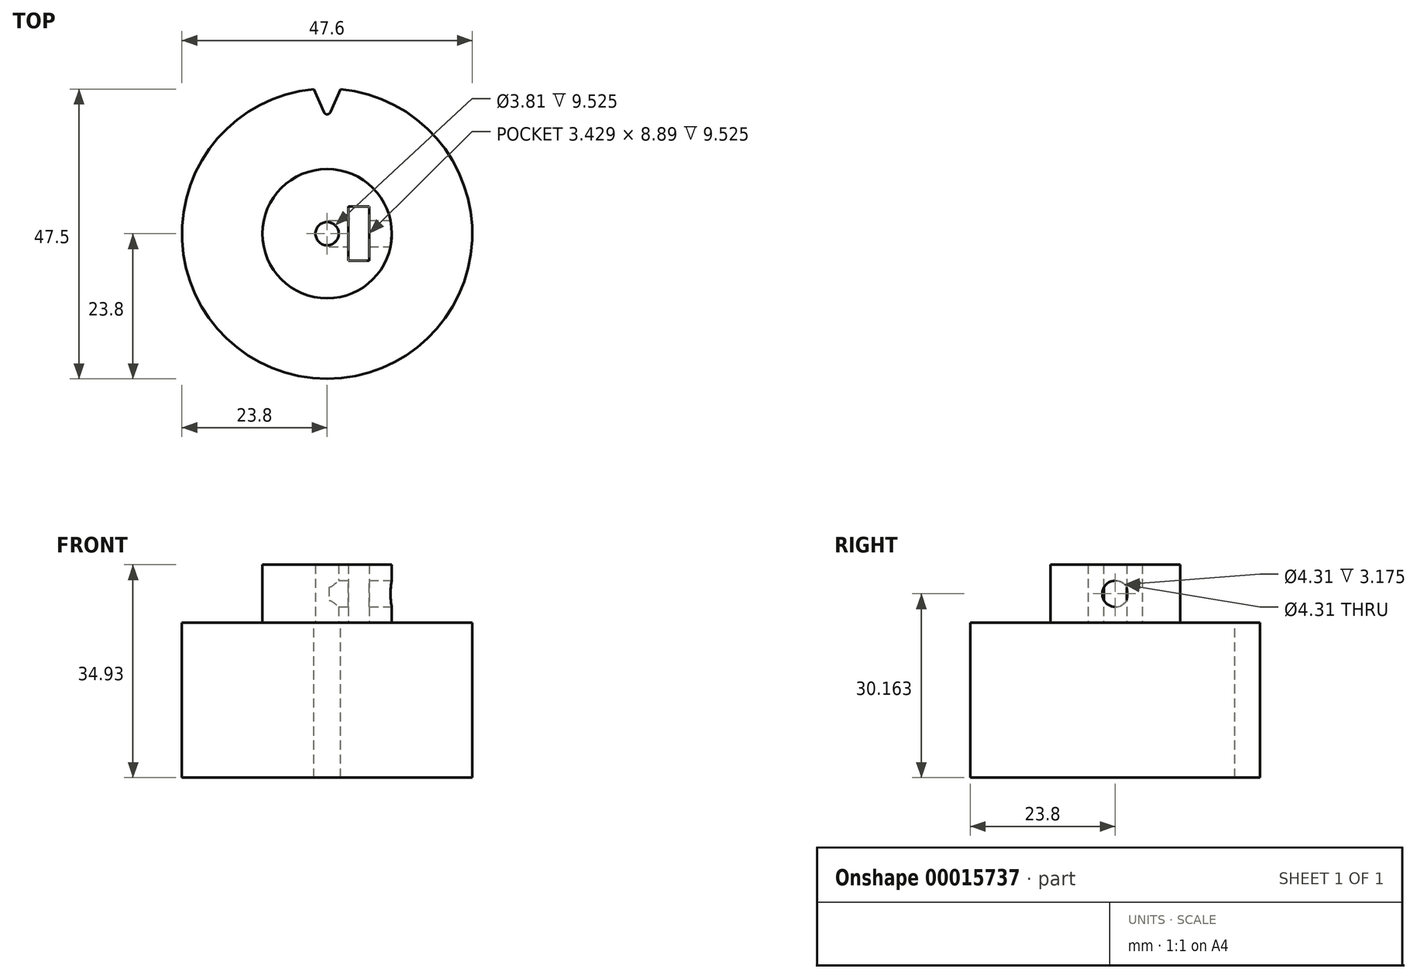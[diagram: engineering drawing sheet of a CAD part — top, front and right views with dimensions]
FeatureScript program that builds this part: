
annotation { "Feature Type Name" : "Feature", "Feature Type Description" : "" }
export const myFeature = defineFeature(function(context is Context, id is Id, definition is map)
    precondition{}
    {
        {
            var Q0;
            Q0=qCreatedBy(makeId("Top.planeOp"),FACE);
            var sketch = newSketch(context, id + "F0", { "sketchPlane" : qUnion([Q0])});
            skCircle(sketch, "E0", {"center": v(0, 0) * mm, "radius": 23.8 * mm});
            skSolve(sketch);
        }
        {
            var Q0;
            Q0 = qSketchRegion(id + "F0", true);
            extrude(context, id + "F1", {"entities" : qUnion([Q0]), "depth" : 25.4 * mm});
        }
        {
            var Q0;
            Q0=makeQuery(id+"F1.opExtrude","CAP_FACE",FACE,{"disambiguationData":[OSD([sQuery(id+"F0.wireOp",EDGE,"E0")])],"isStart":false});
            var sketch = newSketch(context, id + "F2", { "sketchPlane" : qUnion([Q0])});
            skLineSegment(sketch, "E1", {"start": v(0, 0) * mm, "end": v(0, 23.8) * mm, "construction": true});
            skLineSegment(sketch, "E2", {"start": v(0, 0) * mm, "end": v(1.49, 23.76) * mm, "construction": true});
            skArc(sketch, "E3", {"start": v(2.19, 23.7) * mm, "mid": v(0, 23.8) * mm, "end": v(-2.19, 23.7) * mm});
            skLineSegment(sketch, "E4", {"start": v(-2.19, 23.7) * mm, "end": v(-0.55, 19.94) * mm});
            skLineSegment(sketch, "E5", {"start": v(2.19, 23.7) * mm, "end": v(0.55, 19.94) * mm});
            skArc(sketch, "E6", {"start": v(-0.55, 19.94) * mm, "mid": v(0, 19.58) * mm, "end": v(0.55, 19.94) * mm});
            skPoint(sketch, "E7", {"position": v(1.37, 21.82) * mm});
            skSolve(sketch);
        }
        {
            var Q0;
            Q0 = qSketchRegion(id + "F2", true);
            var Q1;
            Q1=makeQuery(id+"F1.opExtrude","CAP_FACE",FACE,{"disambiguationData":[OSD([sQuery(id+"F0.wireOp",EDGE,"E0")])],"isStart":true});
            extrude(context, id + "F3", {"entities" : qUnion([Q0]), "operationType" : NewBodyOperationType.REMOVE, "endBound" : BoundingType.UP_TO_SURFACE, "oppositeDirection" : true, "endBoundEntityFace" : qUnion([Q1]), "depth" : 25.4 * mm});
        }
        {
            var Q0;
            Q0=makeQuery(id+"F1.opExtrude","CAP_FACE",FACE,{"disambiguationData":[OSD([sQuery(id+"F0.wireOp",EDGE,"E0")])],"isStart":false});
            var sketch = newSketch(context, id + "F4", { "sketchPlane" : qUnion([Q0])});
            skCircle(sketch, "E8", {"center": v(0, 0) * mm, "radius": 1.9 * mm});
            skLineSegment(sketch, "E9", {"start": v(0, 0) * mm, "end": v(1.9, 0) * mm, "construction": true});
            skLineSegment(sketch, "E10.bottom", {"start": v(6.92, 4.45) * mm, "end": v(3.5, 4.45) * mm});
            skLineSegment(sketch, "E10.top", {"start": v(6.92, -4.44) * mm, "end": v(3.5, -4.44) * mm});
            skLineSegment(sketch, "E10.left", {"start": v(6.92, 4.44) * mm, "end": v(6.92, -4.44) * mm});
            skLineSegment(sketch, "E10.right", {"start": v(3.5, 4.44) * mm, "end": v(3.5, -4.44) * mm});
            skLineSegment(sketch, "E11", {"start": v(1.9, 0) * mm, "end": v(3.5, 0) * mm, "construction": true});
            skCircle(sketch, "E12", {"center": v(6.92, -4.44) * mm, "radius": 2.38 * mm, "construction": true});
            skCircle(sketch, "E13", {"center": v(0, 0) * mm, "radius": 10.6 * mm});
            skSolve(sketch);
        }
        {
            var Q0;
            Q0 = qSketchRegion(id + "F4", true);
            extrude(context, id + "F5", {"entities" : qUnion([Q0]), "operationType" : NewBodyOperationType.ADD, "depth" : 9.52 * mm});
        }
        {
            var Q0;
            Q0=makeQuery(id+"F5.opExtrude","SWEPT_FACE",FACE,{"disambiguationData":[OSD([sQuery(id+"F4.wireOp",EDGE,"E10.right")])]});
            var sketch = newSketch(context, id + "F6", { "sketchPlane" : qUnion([Q0])});
            skLineSegment(sketch, "E14", {"start": v(0, 34.93) * mm, "end": v(0, 25.4) * mm, "construction": true});
            skCircle(sketch, "E15", {"center": v(0, 30.16) * mm, "radius": 2.15 * mm});
            skSolve(sketch);
        }
        {
            var Q0;
            Q0 = qSketchRegion(id + "F6", true);
            var Q1;
            Q1=makeQuery(id+"F5.opExtrude","SWEPT_FACE",FACE,{"disambiguationData":[OSD([sQuery(id+"F4.wireOp",EDGE,"E8")])]});
            var Q2;
            Q2=makeQuery(id+"F5.opExtrude","SWEPT_FACE",FACE,{"disambiguationData":[OSD([sQuery(id+"F4.wireOp",EDGE,"E13")])]});
            extrude(context, id + "F7", {"entities" : qUnion([Q0]), "operationType" : NewBodyOperationType.REMOVE, "oppositeDirection" : true, "endBoundEntityFace" : qUnion([Q1]), "depth" : 3.17 * mm, "hasSecondDirection" : true, "secondDirectionBound" : BoundingType.UP_TO_SURFACE, "secondDirectionOppositeDirection" : false, "secondDirectionBoundEntityFace" : qUnion([Q2]), "secondDirectionDepth" : 25.4 * mm});
        }
    });
